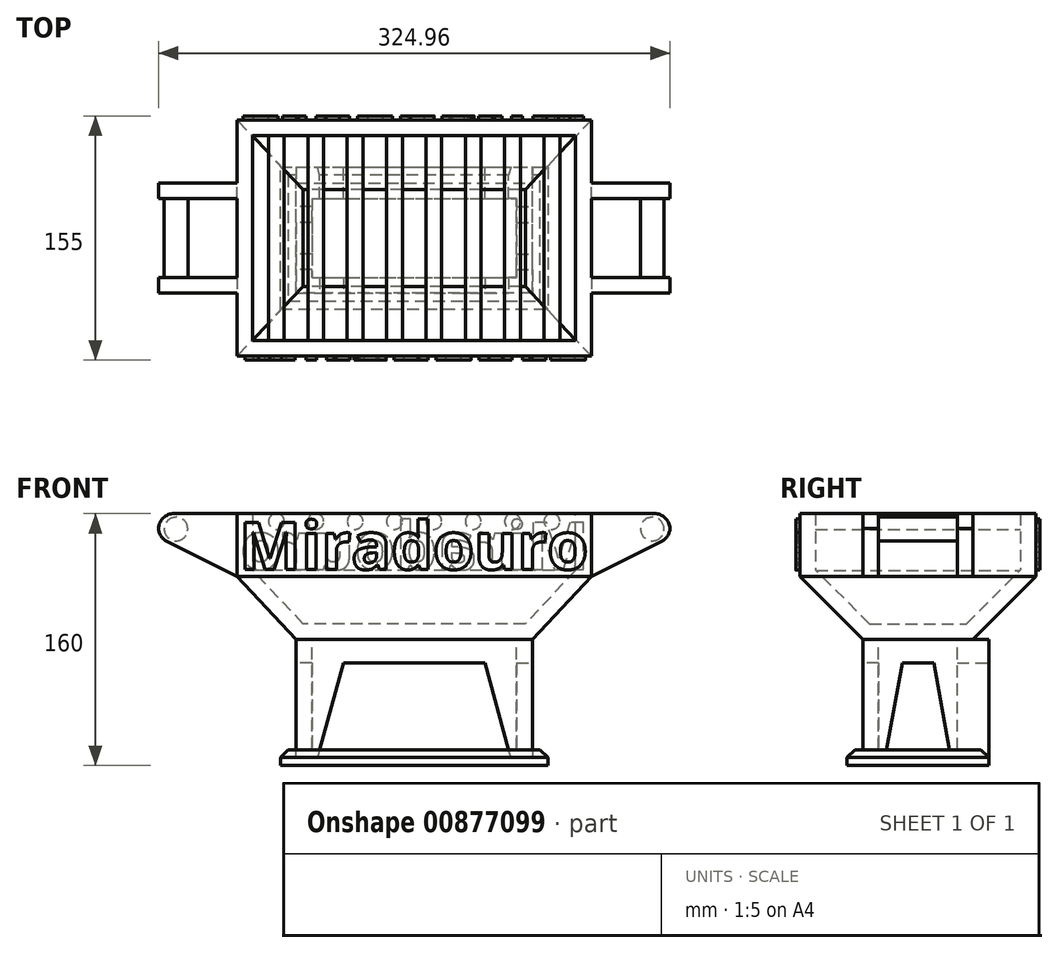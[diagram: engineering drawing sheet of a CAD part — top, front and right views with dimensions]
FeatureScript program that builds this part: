
annotation { "Feature Type Name" : "Feature", "Feature Type Description" : "" }
export const myFeature = defineFeature(function(context is Context, id is Id, definition is map)
    precondition{}
    {
        {
            var Q0;
            Q0=qCreatedBy(makeId("Front.planeOp"),FACE);
            var sketch = newSketch(context, id + "F0", { "sketchPlane" : qUnion([Q0])});
            skLineSegment(sketch, "E0.bottom", {"start": v(-98.2, 60.45) * mm, "end": v(126.8, 60.45) * mm});
            skLineSegment(sketch, "E1", {"start": v(-98.2, 20.45) * mm, "end": v(-60.7, -19.55) * mm});
            skLineSegment(sketch, "E2", {"start": v(126.8, 20.45) * mm, "end": v(89.3, -19.55) * mm});
            skLineSegment(sketch, "E3", {"start": v(-98.2, 60.45) * mm, "end": v(-98.2, 20.45) * mm});
            skLineSegment(sketch, "E4", {"start": v(-60.7, -19.55) * mm, "end": v(89.3, -19.55) * mm});
            skLineSegment(sketch, "E5", {"start": v(126.8, 20.45) * mm, "end": v(126.8, 60.45) * mm});
            skLineSegment(sketch, "E6", {"start": v(-98.2, 20.45) * mm, "end": v(126.8, 20.45) * mm});
            skSolve(sketch);
        }
        {
            var Q0;
            Q0=makeQuery(id+"F0.imprint","IMPRINT",FACE,{"disambiguationData":[TD([[makeQuery(id+"F0.imprint","IMPRINT",EDGE,{"derivedFrom":sQuery(id+"F0.wireOp",EDGE,"E0.bottom")}),-1.0]])]});
            extrude(context, id + "F1", {"entities" : qUnion([Q0]), "depth" : 150 * mm, "offsetDistance" : 25 * mm});
        }
        {
            var Q0;
            Q0=makeQuery(id+"F1.opExtrude","SWEPT_FACE",FACE,{"disambiguationData":[OSD([sQuery(id+"F0.wireOp",EDGE,"E0.bottom")])]});
            shell(context, id + "F2", {"entities" : qUnion([Q0]), "thickness" : 10 * mm});
        }
        {
            var Q0;
            Q0=makeQuery(id+"F0.imprint","IMPRINT",FACE,{"disambiguationData":[TD([[makeQuery(id+"F0.imprint","IMPRINT",EDGE,{"derivedFrom":sQuery(id+"F0.wireOp",EDGE,"E1")}),1.0]])]});
            extrude(context, id + "F3", {"entities" : qUnion([Q0]), "operationType" : NewBodyOperationType.ADD, "depth" : 150 * mm, "offsetDistance" : 25 * mm});
        }
        {
            var Q0;
            Q0=makeQuery(id+"F3.opExtrude","CAP_EDGE",EDGE,{"disambiguationData":[OSD([sQuery(id+"F0.wireOp",EDGE,"E4")])],"isStart":false});
            var Q1;
            Q1=makeQuery(id+"F3.opExtrude","CAP_EDGE",EDGE,{"disambiguationData":[OSD([sQuery(id+"F0.wireOp",EDGE,"E4")])],"isStart":true});
            chamfer(context, id + "F4", {"entities" : qUnion([Q0, Q1]), "width" : 40 * mm, "tangentPropagation" : true});
        }
        {
            var Q0;
            Q0=makeQuery(id+"F2.opShell","OFFSET_FACE",FACE,{"disambiguationData":[OSD([sQuery(id+"F0.wireOp",EDGE,"E6")])]});
            shell(context, id + "F5", {"entities" : qUnion([Q0]), "thickness" : 10 * mm});
        }
        {
            var Q0;
            {var subQ0=sQuery(id+"F0.wireOp",EDGE,"E4");Q0=makeQuery(id+"F4.opChamfer","BLEND_EDGE",EDGE,{"blendedFrom":[makeQuery(id+"F3.opExtrude","CAP_EDGE",EDGE,{"disambiguationData":[OSD([subQ0])],"isStart":false}),makeQuery(id+"F3.opExtrude","SWEPT_FACE",FACE,{"disambiguationData":[OSD([subQ0])]})],"blendedInto":[makeQuery(id+"F3.opExtrude","SWEPT_FACE",FACE,{"disambiguationData":[OSD([subQ0])]})]});}
            cPoint(context, id + "F6", {"entities" : qUnion([Q0]), "parameter" : 0.5});
        }
        {
            var Q0;
            Q0=qCreatedBy(makeId("Front.planeOp"),FACE);
            var Q1;
            Q1 = qCreatedBy(id + "F6" ,VERTEX);
            cPlane(context, id + "F7", {"entities" : qUnion([Q0, Q1]), "cplaneType" : CPlaneType.PLANE_POINT, "offset" : 25 * mm, "width" : 150 * mm, "height" : 150 * mm});
        }
        {
            var Q0;
            Q0=qCreatedBy(id+"F7.planeOp",FACE);
            var sketch = newSketch(context, id + "F8", { "sketchPlane" : qUnion([Q0])});
            skPoint(sketch, "E7.0", {"position": v(-60.7, -19.55) * mm});
            skLineSegment(sketch, "E8", {"start": v(-60.7, -19.55) * mm, "end": v(-60.7, -89.55) * mm});
            skLineSegment(sketch, "E9", {"start": v(-60.7, -89.55) * mm, "end": v(-45.7, -89.55) * mm});
            skPoint(sketch, "E10.0", {"position": v(89.3, -19.55) * mm});
            skLineSegment(sketch, "E11", {"start": v(89.3, -19.55) * mm, "end": v(89.3, -89.55) * mm});
            skLineSegment(sketch, "E12", {"start": v(89.3, -89.55) * mm, "end": v(74.3, -89.55) * mm});
            skLineSegment(sketch, "E13", {"start": v(-45.7, -89.55) * mm, "end": v(-30.7, -34.55) * mm});
            skLineSegment(sketch, "E14", {"start": v(-30.7, -34.55) * mm, "end": v(59.3, -34.55) * mm});
            skLineSegment(sketch, "E15", {"start": v(59.3, -34.55) * mm, "end": v(74.3, -89.55) * mm});
            skLineSegment(sketch, "E16", {"start": v(-60.7, -19.55) * mm, "end": v(89.3, -19.55) * mm});
            skLineSegment(sketch, "E17", {"start": v(-60.7, -89.55) * mm, "end": v(-70.7, -89.55) * mm});
            skLineSegment(sketch, "E18", {"start": v(-70.7, -89.55) * mm, "end": v(-70.7, -99.55) * mm});
            skLineSegment(sketch, "E19.0", {"start": v(99.3, -89.55) * mm, "end": v(99.3, -99.55) * mm});
            skLineSegment(sketch, "E20", {"start": v(-70.7, -99.55) * mm, "end": v(99.3, -99.55) * mm});
            skLineSegment(sketch, "E21", {"start": v(99.3, -89.55) * mm, "end": v(89.3, -89.55) * mm});
            skLineSegment(sketch, "E22", {"start": v(-45.7, -89.55) * mm, "end": v(74.3, -89.55) * mm});
            skSolve(sketch);
        }
        {
            var Q0;
            {var subQ0=sQuery(id+"F0.wireOp",EDGE,"E4");Q0=makeQuery(id+"F4.opChamfer","BLEND_EDGE",EDGE,{"blendedFrom":[makeQuery(id+"F3.opExtrude","CAP_EDGE",EDGE,{"disambiguationData":[OSD([subQ0])],"isStart":true}),makeQuery(id+"F3.opExtrude","SWEPT_FACE",FACE,{"disambiguationData":[OSD([subQ0])]})],"blendedInto":[makeQuery(id+"F3.opExtrude","SWEPT_FACE",FACE,{"disambiguationData":[OSD([subQ0])]})]});}
            cPoint(context, id + "F9", {"entities" : qUnion([Q0]), "parameter" : 0.5});
        }
        {
            var Q0;
            Q0=qCreatedBy(makeId("Front.planeOp"),FACE);
            var Q1;
            Q1 = qCreatedBy(id + "F9" ,VERTEX);
            cPlane(context, id + "F10", {"entities" : qUnion([Q0, Q1]), "cplaneType" : CPlaneType.PLANE_POINT, "offset" : 25 * mm, "width" : 150 * mm, "height" : 150 * mm});
        }
        {
            var Q0;
            Q0=qCreatedBy(id+"F10.planeOp",FACE);
            var sketch = newSketch(context, id + "F11", { "sketchPlane" : qUnion([Q0])});
            skLineSegment(sketch, "E23.0", {"start": v(89.3, -19.55) * mm, "end": v(89.3, -89.55) * mm});
            skLineSegment(sketch, "E24.0", {"start": v(-60.7, -19.55) * mm, "end": v(89.3, -19.55) * mm});
            skLineSegment(sketch, "E25.0", {"start": v(59.3, -34.55) * mm, "end": v(74.3, -89.55) * mm});
            skLineSegment(sketch, "E26.0", {"start": v(-30.7, -34.55) * mm, "end": v(59.3, -34.55) * mm});
            skLineSegment(sketch, "E27.0", {"start": v(-45.7, -89.55) * mm, "end": v(-30.7, -34.55) * mm});
            skLineSegment(sketch, "E28.0", {"start": v(89.3, -89.55) * mm, "end": v(74.3, -89.55) * mm});
            skLineSegment(sketch, "E29.0", {"start": v(-60.7, -19.55) * mm, "end": v(-60.7, -89.55) * mm});
            skLineSegment(sketch, "E30.0", {"start": v(-60.7, -89.55) * mm, "end": v(-45.7, -89.55) * mm});
            skSolve(sketch);
        }
        {
            var Q0;
            Q0=makeQuery(id+"FVLI1C4s14m3Atx_1.boolean.opBoolean","SPLIT",EDGE,{"derivedFrom":makeQuery(id+"F72nnAJw85Nklb2_1.boolean.opBoolean","SPLIT",EDGE,{"derivedFrom":makeQuery(id+"F3.opExtrude","SWEPT_EDGE",EDGE,{"disambiguationData":[OSD([sQuery(id+"F0.wireOp",EDGE,"E1"),sQuery(id+"F0.wireOp",EDGE,"E4")])]})})});
            cPoint(context, id + "F12", {"entities" : qUnion([Q0]), "parameter" : 0.5});
        }
        {
            var Q0;
            Q0=qCreatedBy(makeId("Right.planeOp"),FACE);
            var Q1;
            Q1 = qCreatedBy(id + "F12" ,VERTEX);
            cPlane(context, id + "F13", {"entities" : qUnion([Q0, Q1]), "cplaneType" : CPlaneType.PLANE_POINT, "offset" : 25 * mm, "width" : 150 * mm, "height" : 150 * mm});
        }
        {
            var Q0;
            Q0=qCreatedBy(id+"F13.planeOp",FACE);
            var sketch = newSketch(context, id + "F14", { "sketchPlane" : qUnion([Q0])});
            skPoint(sketch, "E31.0", {"position": v(-40, -19.55) * mm});
            skPoint(sketch, "E32.0", {"position": v(-110, -19.55) * mm});
            skPoint(sketch, "E33.0", {"position": v(-40, -89.55) * mm});
            skPoint(sketch, "E34.0", {"position": v(-110, -89.55) * mm});
            skLineSegment(sketch, "E35", {"start": v(-40, -19.55) * mm, "end": v(-110, -19.55) * mm});
            skLineSegment(sketch, "E36", {"start": v(-110, -89.55) * mm, "end": v(-110, -19.55) * mm});
            skLineSegment(sketch, "E37", {"start": v(-40, -89.55) * mm, "end": v(-40, -19.55) * mm});
            skLineSegment(sketch, "E38", {"start": v(-40, -89.55) * mm, "end": v(-55, -89.55) * mm});
            skLineSegment(sketch, "E39", {"start": v(-65, -34.55) * mm, "end": v(-85, -34.55) * mm});
            skLineSegment(sketch, "E40", {"start": v(-110, -89.55) * mm, "end": v(-95, -89.55) * mm});
            skLineSegment(sketch, "E41", {"start": v(-65, -34.55) * mm, "end": v(-55, -89.55) * mm});
            skLineSegment(sketch, "E42", {"start": v(-85, -34.55) * mm, "end": v(-95, -89.55) * mm});
            skSolve(sketch);
        }
        {
            var Q0;
            Q0=makeQuery(id+"F3.opExtrude","SWEPT_EDGE",EDGE,{"disambiguationData":[OSD([sQuery(id+"F0.wireOp",EDGE,"E2"),sQuery(id+"F0.wireOp",EDGE,"E4")])]});
            cPoint(context, id + "F15", {"entities" : qUnion([Q0]), "parameter" : 0.5});
        }
        {
            var Q0;
            Q0=qCreatedBy(makeId("Right.planeOp"),FACE);
            var Q1;
            Q1 = qCreatedBy(id + "F15" ,VERTEX);
            cPlane(context, id + "F16", {"entities" : qUnion([Q0, Q1]), "cplaneType" : CPlaneType.PLANE_POINT, "offset" : 25 * mm, "width" : 150 * mm, "height" : 150 * mm});
        }
        {
            var Q0;
            Q0=qCreatedBy(id+"F16.planeOp",FACE);
            var sketch = newSketch(context, id + "F17", { "sketchPlane" : qUnion([Q0])});
            skLineSegment(sketch, "E43.0.0", {"start": v(-85, -34.55) * mm, "end": v(-65, -34.55) * mm});
            skLineSegment(sketch, "E43.0.1", {"start": v(-65, -34.55) * mm, "end": v(-55, -89.55) * mm});
            skLineSegment(sketch, "E43.0.2", {"start": v(-55, -89.55) * mm, "end": v(-40, -89.55) * mm});
            skLineSegment(sketch, "E43.0.3", {"start": v(-40, -89.55) * mm, "end": v(-40, -19.55) * mm});
            skLineSegment(sketch, "E43.0.4", {"start": v(-40, -19.55) * mm, "end": v(-110, -19.55) * mm});
            skLineSegment(sketch, "E43.0.5", {"start": v(-110, -19.55) * mm, "end": v(-110, -89.55) * mm});
            skLineSegment(sketch, "E43.0.6", {"start": v(-110, -89.55) * mm, "end": v(-95, -89.55) * mm});
            skLineSegment(sketch, "E43.0.7", {"start": v(-95, -89.55) * mm, "end": v(-85, -34.55) * mm});
            skSolve(sketch);
        }
        {
            var Q0;
            Q0=makeQuery(id+"F8.imprint","IMPRINT",FACE,{"disambiguationData":[TD([[makeQuery(id+"F8.imprint","IMPRINT",EDGE,{"derivedFrom":sQuery(id+"F8.wireOp",EDGE,"E8")}),1.0]])]});
            extrude(context, id + "F18", {"entities" : qUnion([Q0]), "operationType" : NewBodyOperationType.ADD, "oppositeDirection" : true, "depth" : 10 * mm, "offsetDistance" : 25 * mm});
        }
        {
            var Q0;
            Q0=makeQuery(id+"F11.imprint","IMPRINT",FACE,{"disambiguationData":[TD([[makeQuery(id+"F11.imprint","IMPRINT",EDGE,{"derivedFrom":sQuery(id+"F11.wireOp",EDGE,"E23.0")}),-1.0]])]});
            extrude(context, id + "F19", {"entities" : qUnion([Q0]), "operationType" : NewBodyOperationType.ADD, "depth" : 10 * mm, "offsetDistance" : 25 * mm});
        }
        {
            var Q0;
            Q0=makeQuery(id+"F14.imprint","IMPRINT",FACE,{"disambiguationData":[TD([[makeQuery(id+"F14.imprint","IMPRINT",EDGE,{"derivedFrom":sQuery(id+"F14.wireOp",EDGE,"E35")}),1.0]])]});
            extrude(context, id + "F20", {"entities" : qUnion([Q0]), "operationType" : NewBodyOperationType.ADD, "depth" : 10 * mm, "offsetDistance" : 25 * mm});
        }
        {
            var Q0;
            Q0=makeQuery(id+"F17.imprint","IMPRINT",FACE,{"disambiguationData":[TD([[makeQuery(id+"F17.imprint","IMPRINT",EDGE,{"derivedFrom":sQuery(id+"F17.wireOp",EDGE,"E43.0.0")}),1.0]])]});
            extrude(context, id + "F21", {"entities" : qUnion([Q0]), "operationType" : NewBodyOperationType.ADD, "oppositeDirection" : true, "depth" : 10 * mm, "offsetDistance" : 25 * mm});
        }
        {
            var Q0;
            Q0=makeQuery(id+"F18.opExtrude","CAP_FACE",FACE,{"disambiguationData":[OSD([sQuery(id+"F8.wireOp",EDGE,"E8"),sQuery(id+"F8.wireOp",EDGE,"E9"),sQuery(id+"F8.wireOp",EDGE,"E11"),sQuery(id+"F8.wireOp",EDGE,"E12"),sQuery(id+"F8.wireOp",EDGE,"E13"),sQuery(id+"F8.wireOp",EDGE,"E14"),sQuery(id+"F8.wireOp",EDGE,"E15"),sQuery(id+"F8.wireOp",EDGE,"E16")])],"isStart":true});
            cPlane(context, id + "F22", {"entities" : qUnion([Q0]), "cplaneType" : CPlaneType.OFFSET, "offset" : 0 * mm, "width" : 150 * mm, "height" : 150 * mm});
        }
        {
            var Q0;
            Q0=qCreatedBy(id+"F22.planeOp",FACE);
            var sketch = newSketch(context, id + "F23", { "sketchPlane" : qUnion([Q0])});
            skLineSegment(sketch, "E44.0", {"start": v(-98.2, 60.45) * mm, "end": v(-98.2, 20.45) * mm});
            skLineSegment(sketch, "E45", {"start": v(-98.2, 60.45) * mm, "end": v(-148.2, 60.45) * mm});
            skLineSegment(sketch, "E46", {"start": v(-148.2, 60.45) * mm, "end": v(-148.2, 45.45) * mm});
            skLineSegment(sketch, "E47", {"start": v(-148.2, 45.45) * mm, "end": v(-98.2, 20.45) * mm});
            skLineSegment(sketch, "E48.0", {"start": v(126.8, 20.45) * mm, "end": v(126.8, 60.45) * mm});
            skLineSegment(sketch, "E49", {"start": v(126.8, 60.45) * mm, "end": v(176.8, 60.45) * mm});
            skLineSegment(sketch, "E50", {"start": v(176.8, 60.45) * mm, "end": v(176.8, 45.45) * mm});
            skLineSegment(sketch, "E51", {"start": v(176.8, 45.45) * mm, "end": v(126.8, 20.45) * mm});
            skSolve(sketch);
        }
        {
            var Q0;
            Q0=makeQuery(id+"F19.opExtrude","CAP_FACE",FACE,{"disambiguationData":[OSD([sQuery(id+"F11.wireOp",EDGE,"E23.0"),sQuery(id+"F11.wireOp",EDGE,"E24.0"),sQuery(id+"F11.wireOp",EDGE,"E25.0"),sQuery(id+"F11.wireOp",EDGE,"E26.0"),sQuery(id+"F11.wireOp",EDGE,"E27.0"),sQuery(id+"F11.wireOp",EDGE,"E28.0"),sQuery(id+"F11.wireOp",EDGE,"E29.0"),sQuery(id+"F11.wireOp",EDGE,"E30.0")])],"isStart":true});
            cPlane(context, id + "F24", {"entities" : qUnion([Q0]), "cplaneType" : CPlaneType.OFFSET, "offset" : 0 * mm, "width" : 150 * mm, "height" : 150 * mm});
        }
        {
            var Q0;
            Q0=qCreatedBy(id+"F24.planeOp",FACE);
            var sketch = newSketch(context, id + "F25", { "sketchPlane" : qUnion([Q0])});
            skLineSegment(sketch, "E52.0.0", {"start": v(148.2, 60.45) * mm, "end": v(148.2, 45.45) * mm});
            skLineSegment(sketch, "E52.0.1", {"start": v(148.2, 45.45) * mm, "end": v(98.2, 20.45) * mm});
            skLineSegment(sketch, "E52.0.2", {"start": v(98.2, 20.45) * mm, "end": v(98.2, 60.45) * mm});
            skLineSegment(sketch, "E52.0.3", {"start": v(98.2, 60.45) * mm, "end": v(148.2, 60.45) * mm});
            skLineSegment(sketch, "E53.0.0", {"start": v(-126.8, 20.45) * mm, "end": v(-176.8, 45.45) * mm});
            skLineSegment(sketch, "E53.0.1", {"start": v(-176.8, 45.45) * mm, "end": v(-176.8, 60.45) * mm});
            skLineSegment(sketch, "E53.0.2", {"start": v(-176.8, 60.45) * mm, "end": v(-126.8, 60.45) * mm});
            skLineSegment(sketch, "E53.0.3", {"start": v(-126.8, 60.45) * mm, "end": v(-126.8, 20.45) * mm});
            skSolve(sketch);
        }
        {
            var Q0;
            Q0=makeQuery(id+"F23.imprint","IMPRINT",FACE,{"disambiguationData":[TD([[makeQuery(id+"F23.imprint","IMPRINT",EDGE,{"derivedFrom":sQuery(id+"F23.wireOp",EDGE,"E48.0")}),-1.0]])]});
            var Q1;
            Q1=makeQuery(id+"F23.imprint","IMPRINT",FACE,{"disambiguationData":[TD([[makeQuery(id+"F23.imprint","IMPRINT",EDGE,{"derivedFrom":sQuery(id+"F23.wireOp",EDGE,"E44.0")}),-1.0]])]});
            extrude(context, id + "F26", {"entities" : qUnion([Q0, Q1]), "operationType" : NewBodyOperationType.ADD, "oppositeDirection" : true, "depth" : 10 * mm, "offsetDistance" : 25 * mm});
        }
        {
            var Q0;
            Q0=makeQuery(id+"F25.imprint","IMPRINT",FACE,{"disambiguationData":[TD([[makeQuery(id+"F25.imprint","IMPRINT",EDGE,{"derivedFrom":sQuery(id+"F25.wireOp",EDGE,"E53.0.0")}),-1.0]])]});
            var Q1;
            Q1=makeQuery(id+"F25.imprint","IMPRINT",FACE,{"disambiguationData":[TD([[makeQuery(id+"F25.imprint","IMPRINT",EDGE,{"derivedFrom":sQuery(id+"F25.wireOp",EDGE,"E52.0.0")}),-1.0]])]});
            extrude(context, id + "F27", {"entities" : qUnion([Q0, Q1]), "operationType" : NewBodyOperationType.ADD, "oppositeDirection" : true, "depth" : 10 * mm, "offsetDistance" : 25 * mm});
        }
        {
            var Q0;
            Q0=makeQuery(id+"F27.opExtrude","CAP_FACE",FACE,{"disambiguationData":[OSD([sQuery(id+"F25.wireOp",EDGE,"E52.0.0"),sQuery(id+"F25.wireOp",EDGE,"E52.0.1"),sQuery(id+"F25.wireOp",EDGE,"E52.0.2"),sQuery(id+"F25.wireOp",EDGE,"E52.0.3")])],"isStart":false});
            cPlane(context, id + "F28", {"entities" : qUnion([Q0]), "cplaneType" : CPlaneType.OFFSET, "offset" : 0 * mm, "width" : 150 * mm, "height" : 150 * mm});
        }
        {
            var Q0;
            Q0=makeQuery(id+"F26.opExtrude","CAP_FACE",FACE,{"disambiguationData":[OSD([sQuery(id+"F23.wireOp",EDGE,"E44.0"),sQuery(id+"F23.wireOp",EDGE,"E45"),sQuery(id+"F23.wireOp",EDGE,"E46"),sQuery(id+"F23.wireOp",EDGE,"E47")])],"isStart":false});
            cPlane(context, id + "F29", {"entities" : qUnion([Q0]), "cplaneType" : CPlaneType.OFFSET, "offset" : 0 * mm, "width" : 150 * mm, "height" : 150 * mm});
        }
        {
            var Q0;
            Q0=qCreatedBy(id+"F28.planeOp",FACE);
            var sketch = newSketch(context, id + "F30", { "sketchPlane" : qUnion([Q0])});
            skCircle(sketch, "E54", {"center": v(-136.94, 50.65) * mm, "radius": 7.5 * mm});
            skCircle(sketch, "E55", {"center": v(165.56, 50.65) * mm, "radius": 7.5 * mm});
            skSolve(sketch);
        }
        {
            var Q0;
            Q0=makeQuery(id+"F27.opExtrude","SWEPT_EDGE",EDGE,{"disambiguationData":[OSD([sQuery(id+"F25.wireOp",EDGE,"E52.0.0"),sQuery(id+"F25.wireOp",EDGE,"E52.0.3")])]});
            var Q1;
            Q1=makeQuery(id+"F27.opExtrude","SWEPT_EDGE",EDGE,{"disambiguationData":[OSD([sQuery(id+"F25.wireOp",EDGE,"E52.0.0"),sQuery(id+"F25.wireOp",EDGE,"E52.0.1")])]});
            var Q2;
            Q2=makeQuery(id+"F26.opExtrude","SWEPT_EDGE",EDGE,{"disambiguationData":[OSD([sQuery(id+"F23.wireOp",EDGE,"E46"),sQuery(id+"F23.wireOp",EDGE,"E47")])]});
            var Q3;
            Q3=makeQuery(id+"F26.opExtrude","SWEPT_EDGE",EDGE,{"disambiguationData":[OSD([sQuery(id+"F23.wireOp",EDGE,"E45"),sQuery(id+"F23.wireOp",EDGE,"E46")])]});
            var Q4;
            Q4=makeQuery(id+"F26.opExtrude","SWEPT_EDGE",EDGE,{"disambiguationData":[OSD([sQuery(id+"F23.wireOp",EDGE,"E49"),sQuery(id+"F23.wireOp",EDGE,"E50")])]});
            var Q5;
            Q5=makeQuery(id+"F26.opExtrude","SWEPT_EDGE",EDGE,{"disambiguationData":[OSD([sQuery(id+"F23.wireOp",EDGE,"E50"),sQuery(id+"F23.wireOp",EDGE,"E51")])]});
            var Q6;
            Q6=makeQuery(id+"F27.opExtrude","SWEPT_EDGE",EDGE,{"disambiguationData":[OSD([sQuery(id+"F25.wireOp",EDGE,"E53.0.0"),sQuery(id+"F25.wireOp",EDGE,"E53.0.1")])]});
            var Q7;
            Q7=makeQuery(id+"F27.opExtrude","SWEPT_EDGE",EDGE,{"disambiguationData":[OSD([sQuery(id+"F25.wireOp",EDGE,"E53.0.1"),sQuery(id+"F25.wireOp",EDGE,"E53.0.2")])]});
            fillet(context, id + "F31", {"entities" : qUnion([Q0, Q1, Q2, Q3, Q4, Q5, Q6, Q7]), "radius" : 10 * mm, "tangentPropagation" : true, "allowEdgeOverflow" : false});
        }
        {
            var Q0;
            Q0=makeQuery(id+"F30.imprint","IMPRINT",FACE,{"disambiguationData":[TD([[makeQuery(id+"F30.imprint","IMPRINT",EDGE,{"derivedFrom":sQuery(id+"F30.wireOp",EDGE,"E54")}),1.0]])]});
            var Q1;
            Q1=makeQuery(id+"F30.imprint","IMPRINT",FACE,{"disambiguationData":[TD([[makeQuery(id+"F30.imprint","IMPRINT",EDGE,{"derivedFrom":sQuery(id+"F30.wireOp",EDGE,"E55")}),1.0]])]});
            extrude(context, id + "F32", {"entities" : qUnion([Q0, Q1]), "operationType" : NewBodyOperationType.ADD, "depth" : 60 * mm, "offsetDistance" : 25 * mm});
        }
        {
            var Q0;
            Q0=qCreatedBy(makeId("Front.planeOp"),FACE);
            var sketch = newSketch(context, id + "F33", { "sketchPlane" : qUnion([Q0])});
            skLineSegment(sketch, "E56.0.0", {"start": v(-98.2, 60.45) * mm, "end": v(-98.2, 20.45) * mm});
            skLineSegment(sketch, "E56.0.1", {"start": v(-98.2, 20.45) * mm, "end": v(126.8, 20.45) * mm});
            skLineSegment(sketch, "E56.0.2", {"start": v(126.8, 20.45) * mm, "end": v(126.8, 60.45) * mm});
            skLineSegment(sketch, "E56.0.3", {"start": v(126.8, 60.45) * mm, "end": v(-98.2, 60.45) * mm});
            skCircle(sketch, "E57", {"center": v(101.8, 55.45) * mm, "radius": 5 * mm});
            skCircle(sketch, "E58.1.0.0", {"center": v(76.8, 55.45) * mm, "radius": 5 * mm});
            skCircle(sketch, "E58.2.0.0", {"center": v(51.8, 55.45) * mm, "radius": 5 * mm});
            skCircle(sketch, "E58.3.0.0", {"center": v(26.8, 55.45) * mm, "radius": 5 * mm});
            skCircle(sketch, "E58.4.0.0", {"center": v(1.8, 55.45) * mm, "radius": 5 * mm});
            skCircle(sketch, "E58.5.0.0", {"center": v(-23.2, 55.45) * mm, "radius": 5 * mm});
            skCircle(sketch, "E58.6.0.0", {"center": v(-48.2, 55.45) * mm, "radius": 5 * mm});
            skCircle(sketch, "E58.7.0.0", {"center": v(-73.2, 55.45) * mm, "radius": 5 * mm});
            skLineSegment(sketch, "E58.direction1", {"start": v(101.8, 55.45) * mm, "end": v(76.8, 55.45) * mm, "construction": true});
            skSolve(sketch);
        }
        {
            var Q0;
            Q0=makeQuery(id+"F33.imprint","IMPRINT",FACE,{"disambiguationData":[TD([[makeQuery(id+"F33.imprint","IMPRINT",EDGE,{"derivedFrom":sQuery(id+"F33.wireOp",EDGE,"E57")}),1.0]])]});
            var Q1;
            Q1=makeQuery(id+"F33.imprint","IMPRINT",FACE,{"disambiguationData":[TD([[makeQuery(id+"F33.imprint","IMPRINT",EDGE,{"derivedFrom":sQuery(id+"F33.wireOp",EDGE,"E58.1.0.0")}),1.0]])]});
            var Q2;
            Q2=makeQuery(id+"F33.imprint","IMPRINT",FACE,{"disambiguationData":[TD([[makeQuery(id+"F33.imprint","IMPRINT",EDGE,{"derivedFrom":sQuery(id+"F33.wireOp",EDGE,"E58.2.0.0")}),1.0]])]});
            var Q3;
            Q3=makeQuery(id+"F33.imprint","IMPRINT",FACE,{"disambiguationData":[TD([[makeQuery(id+"F33.imprint","IMPRINT",EDGE,{"derivedFrom":sQuery(id+"F33.wireOp",EDGE,"E58.3.0.0")}),1.0]])]});
            var Q4;
            Q4=makeQuery(id+"F33.imprint","IMPRINT",FACE,{"disambiguationData":[TD([[makeQuery(id+"F33.imprint","IMPRINT",EDGE,{"derivedFrom":sQuery(id+"F33.wireOp",EDGE,"E58.4.0.0")}),1.0]])]});
            var Q5;
            Q5=makeQuery(id+"F33.imprint","IMPRINT",FACE,{"disambiguationData":[TD([[makeQuery(id+"F33.imprint","IMPRINT",EDGE,{"derivedFrom":sQuery(id+"F33.wireOp",EDGE,"E58.5.0.0")}),1.0]])]});
            var Q6;
            Q6=makeQuery(id+"F33.imprint","IMPRINT",FACE,{"disambiguationData":[TD([[makeQuery(id+"F33.imprint","IMPRINT",EDGE,{"derivedFrom":sQuery(id+"F33.wireOp",EDGE,"E58.6.0.0")}),1.0]])]});
            var Q7;
            Q7=makeQuery(id+"F33.imprint","IMPRINT",FACE,{"disambiguationData":[TD([[makeQuery(id+"F33.imprint","IMPRINT",EDGE,{"derivedFrom":sQuery(id+"F33.wireOp",EDGE,"E58.7.0.0")}),1.0]])]});
            extrude(context, id + "F34", {"entities" : qUnion([Q0, Q1, Q2, Q3, Q4, Q5, Q6, Q7]), "operationType" : NewBodyOperationType.ADD, "depth" : 150 * mm, "offsetDistance" : 25 * mm});
        }
        {
            var Q0;
            Q0=makeQuery(id+"F8.imprint","IMPRINT",FACE,{"disambiguationData":[TD([[makeQuery(id+"F8.imprint","IMPRINT",EDGE,{"derivedFrom":sQuery(id+"F8.wireOp",EDGE,"E9")}),-1.0]])]});
            extrude(context, id + "F35", {"entities" : qUnion([Q0]), "oppositeDirection" : true, "depth" : 70 * mm, "offsetDistance" : 25 * mm});
        }
        {
            var Q0;
            Q0=makeQuery(id+"F35.opExtrude","CAP_FACE",FACE,{"disambiguationData":[OSD([sQuery(id+"F8.wireOp",EDGE,"E9"),sQuery(id+"F8.wireOp",EDGE,"E12"),sQuery(id+"F8.wireOp",EDGE,"E17"),sQuery(id+"F8.wireOp",EDGE,"E18"),sQuery(id+"F8.wireOp",EDGE,"E19.0"),sQuery(id+"F8.wireOp",EDGE,"E20"),sQuery(id+"F8.wireOp",EDGE,"E21"),sQuery(id+"F8.wireOp",EDGE,"E22")])],"isStart":true});
            extrude(context, id + "F36", {"entities" : qUnion([Q0]), "operationType" : NewBodyOperationType.ADD, "depth" : 10 * mm, "offsetDistance" : 25 * mm});
        }
        {
            var Q0;
            Q0=makeQuery(id+"F35.opExtrude","CAP_FACE",FACE,{"disambiguationData":[OSD([sQuery(id+"F8.wireOp",EDGE,"E9"),sQuery(id+"F8.wireOp",EDGE,"E12"),sQuery(id+"F8.wireOp",EDGE,"E17"),sQuery(id+"F8.wireOp",EDGE,"E18"),sQuery(id+"F8.wireOp",EDGE,"E19.0"),sQuery(id+"F8.wireOp",EDGE,"E20"),sQuery(id+"F8.wireOp",EDGE,"E21"),sQuery(id+"F8.wireOp",EDGE,"E22")])],"isStart":false});
            extrude(context, id + "F37", {"entities" : qUnion([Q0]), "operationType" : NewBodyOperationType.ADD, "depth" : 10 * mm, "offsetDistance" : 25 * mm});
        }
        {
            var Q0;
            {var subQ0=sQuery(id+"F0.wireOp",EDGE,"E6");var subQ1=sQuery(id+"F0.wireOp",EDGE,"E4");Q0=makeQuery(id+"F4.opChamfer","BLEND_EDGE",EDGE,{"blendedFrom":[makeQuery(id+"F3.opExtrude","CAP_EDGE",EDGE,{"disambiguationData":[OSD([subQ1])],"isStart":false}),makeQuery(id+"F3.boolean.opBoolean","MERGE",FACE,{"derivedFrom":[makeQuery(id+"F1.opExtrude","CAP_FACE",FACE,{"disambiguationData":[OSD([sQuery(id+"F0.wireOp",EDGE,"E0.bottom"),sQuery(id+"F0.wireOp",EDGE,"E3"),sQuery(id+"F0.wireOp",EDGE,"E5"),subQ0])],"isStart":false}),makeQuery(id+"F3.opExtrude","CAP_FACE",FACE,{"disambiguationData":[OSD([sQuery(id+"F0.wireOp",EDGE,"E1"),sQuery(id+"F0.wireOp",EDGE,"E2"),subQ1,subQ0])],"isStart":false})]})],"blendedInto":[makeQuery(id+"F3.boolean.opBoolean","MERGE",FACE,{"derivedFrom":[makeQuery(id+"F1.opExtrude","CAP_FACE",FACE,{"disambiguationData":[OSD([sQuery(id+"F0.wireOp",EDGE,"E0.bottom"),sQuery(id+"F0.wireOp",EDGE,"E3"),sQuery(id+"F0.wireOp",EDGE,"E5"),subQ0])],"isStart":false}),makeQuery(id+"F3.opExtrude","CAP_FACE",FACE,{"disambiguationData":[OSD([sQuery(id+"F0.wireOp",EDGE,"E1"),sQuery(id+"F0.wireOp",EDGE,"E2"),subQ1,subQ0])],"isStart":false})]})]});}
            cPoint(context, id + "F38", {"entities" : qUnion([Q0]), "parameter" : 0.5});
        }
        {
            var Q0;
            Q0=qCreatedBy(makeId("Front.planeOp"),FACE);
            var Q1;
            Q1 = qCreatedBy(id + "F38" ,VERTEX);
            cPlane(context, id + "F39", {"entities" : qUnion([Q0, Q1]), "cplaneType" : CPlaneType.PLANE_POINT, "offset" : 25 * mm, "width" : 150 * mm, "height" : 150 * mm});
        }
        {
            var Q0;
            Q0=qCreatedBy(id+"F39.planeOp",FACE);
            var sketch = newSketch(context, id + "F40", { "sketchPlane" : qUnion([Q0])});
            skText(sketch, "E59", { "text": "Miradouro", "fontName": "OpenSans-Bold.ttf"});
            const initialGuessF40  = {"E59": [-0.09697, 0.025, 1, 0, 0.0302]};
            skSetInitialGuess(sketch, initialGuessF40);
            skSolve(sketch);
        }
        {
            var Q0;
            Q0 = qSketchRegion(id + "F40", true);
            extrude(context, id + "F41", {"entities" : qUnion([Q0]), "operationType" : NewBodyOperationType.ADD, "depth" : 2.5 * mm, "offsetDistance" : 25 * mm});
        }
        {
            var Q0;
            Q0=makeQuery(id+"F37.opExtrude","CAP_FACE",FACE,{"disambiguationData":[OSD([sQuery(id+"F8.wireOp",EDGE,"E9"),sQuery(id+"F8.wireOp",EDGE,"E12"),sQuery(id+"F8.wireOp",EDGE,"E17"),sQuery(id+"F8.wireOp",EDGE,"E18"),sQuery(id+"F8.wireOp",EDGE,"E19.0"),sQuery(id+"F8.wireOp",EDGE,"E20"),sQuery(id+"F8.wireOp",EDGE,"E21"),sQuery(id+"F8.wireOp",EDGE,"E22")])],"isStart":false});
            cPlane(context, id + "F42", {"entities" : qUnion([Q0]), "cplaneType" : CPlaneType.OFFSET, "offset" : 30 * mm, "width" : 150 * mm, "height" : 150 * mm});
        }
        {
            var Q0;
            Q0=qCreatedBy(id+"F42.planeOp",FACE);
            var sketch = newSketch(context, id + "F43", { "sketchPlane" : qUnion([Q0])});
            skText(sketch, "E60", { "text": "Miradouro", "fontName": "OpenSans-Bold.ttf"});
            const initialGuessF43  = {"E60": [-0.12559, 0.025, 1, 0, 0.0302]};
            skSetInitialGuess(sketch, initialGuessF43);
            skSolve(sketch);
        }
        {
            var Q0;
            {var subQ0=sQuery(id+"F8.wireOp",EDGE,"E18");var subQ1=sQuery(id+"F8.wireOp",EDGE,"E17");Q0=makeQuery(id+"F37.boolean.opBoolean","MERGE",EDGE,{"derivedFrom":[makeQuery(id+"F36.boolean.opBoolean","MERGE",EDGE,{"derivedFrom":[makeQuery(id+"F35.opExtrude","SWEPT_EDGE",EDGE,{"disambiguationData":[OSD([subQ1,subQ0])]}),makeQuery(id+"F36.opExtrude","SWEPT_EDGE",EDGE,{"disambiguationData":[OSD([subQ1,subQ0])]})]}),makeQuery(id+"F37.opExtrude","SWEPT_EDGE",EDGE,{"disambiguationData":[OSD([subQ1,subQ0])]})]});}
            var Q1;
            Q1=makeQuery(id+"F37.opExtrude","CAP_EDGE",EDGE,{"disambiguationData":[OSD([sQuery(id+"F8.wireOp",EDGE,"E9"),sQuery(id+"F8.wireOp",EDGE,"E12"),sQuery(id+"F8.wireOp",EDGE,"E17"),sQuery(id+"F8.wireOp",EDGE,"E21"),sQuery(id+"F8.wireOp",EDGE,"E22")])],"isStart":false});
            var Q2;
            Q2=makeQuery(id+"F36.opExtrude","CAP_EDGE",EDGE,{"disambiguationData":[OSD([sQuery(id+"F8.wireOp",EDGE,"E9"),sQuery(id+"F8.wireOp",EDGE,"E12"),sQuery(id+"F8.wireOp",EDGE,"E17"),sQuery(id+"F8.wireOp",EDGE,"E21"),sQuery(id+"F8.wireOp",EDGE,"E22")])],"isStart":false});
            var Q3;
            {var subQ0=sQuery(id+"F8.wireOp",EDGE,"E21");var subQ1=sQuery(id+"F8.wireOp",EDGE,"E19.0");Q3=makeQuery(id+"F37.boolean.opBoolean","MERGE",EDGE,{"derivedFrom":[makeQuery(id+"F36.boolean.opBoolean","MERGE",EDGE,{"derivedFrom":[makeQuery(id+"F35.opExtrude","SWEPT_EDGE",EDGE,{"disambiguationData":[OSD([subQ1,subQ0])]}),makeQuery(id+"F36.opExtrude","SWEPT_EDGE",EDGE,{"disambiguationData":[OSD([subQ1,subQ0])]})]}),makeQuery(id+"F37.opExtrude","SWEPT_EDGE",EDGE,{"disambiguationData":[OSD([subQ1,subQ0])]})]});}
            chamfer(context, id + "F44", {"entities" : qUnion([Q0, Q1, Q2, Q3]), "width" : 5 * mm, "tangentPropagation" : true});
        }
        {
            var Q0;
            Q0 = qSketchRegion(id + "F43", true);
            extrude(context, id + "F45", {"entities" : qUnion([Q0]), "operationType" : NewBodyOperationType.ADD, "depth" : 2.5 * mm, "offsetDistance" : 25 * mm});
        }
    });
